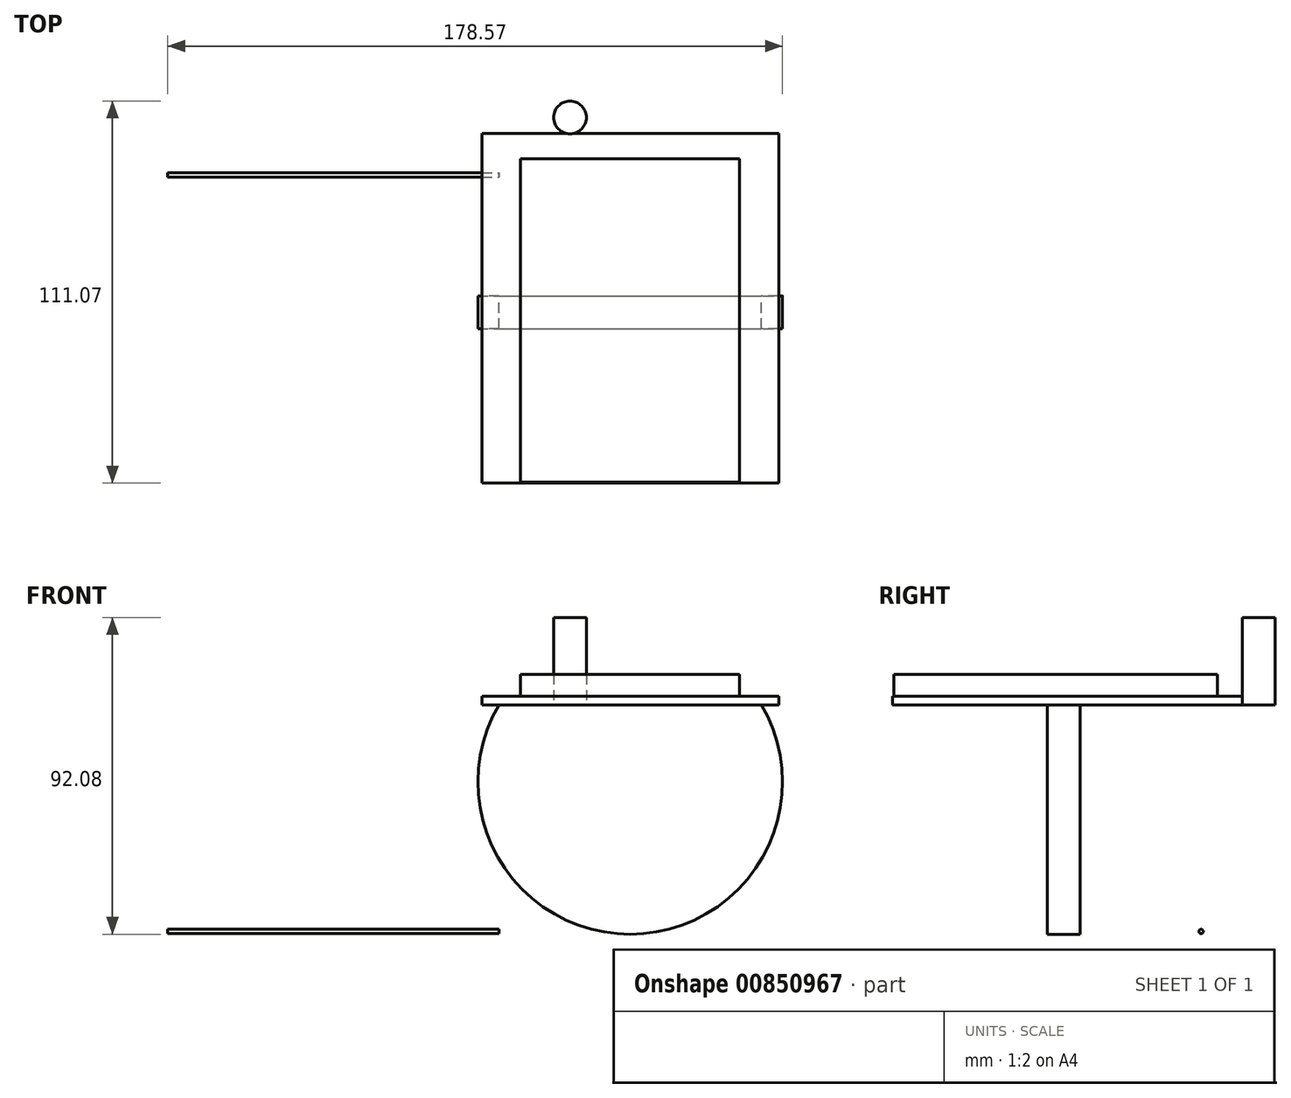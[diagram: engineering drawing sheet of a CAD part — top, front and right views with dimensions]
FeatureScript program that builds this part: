
annotation { "Feature Type Name" : "Feature", "Feature Type Description" : "" }
export const myFeature = defineFeature(function(context is Context, id is Id, definition is map)
    precondition{}
    {
        {
            var Q0;
            Q0=qCreatedBy(makeId("Front.planeOp"),FACE);
            var sketch = newSketch(context, id + "F0", { "sketchPlane" : qUnion([Q0])});
            skArc(sketch, "E0", {"start": v(0, 0) * mm, "mid": v(38.09, -66.68) * mm, "end": v(76.17, 0) * mm});
            skLineSegment(sketch, "E1", {"start": v(0, 0) * mm, "end": v(76.17, 0) * mm});
            skSolve(sketch);
        }
        {
            var Q0;
            Q0 = qSketchRegion(id + "F0", true);
            extrude(context, id + "F1", {"entities" : qUnion([Q0]), "depth" : 9.52 * mm, "offsetDistance" : 25.4 * mm});
        }
        {
            var Q0;
            Q0=makeQuery(id+"F1.opExtrude","SWEPT_FACE",FACE,{"disambiguationData":[OSD([sQuery(id+"F0.wireOp",EDGE,"E1")])]});
            var sketch = newSketch(context, id + "F2", { "sketchPlane" : qUnion([Q0])});
            skLineSegment(sketch, "E2.bottom", {"start": v(81.21, -54.44) * mm, "end": v(-5.02, -54.44) * mm});
            skLineSegment(sketch, "E2.top", {"start": v(81.21, 47.16) * mm, "end": v(-5.02, 47.16) * mm});
            skLineSegment(sketch, "E2.left", {"start": v(81.21, -54.44) * mm, "end": v(81.21, 47.16) * mm});
            skLineSegment(sketch, "E2.right", {"start": v(-5.02, -54.44) * mm, "end": v(-5.02, 47.16) * mm});
            skSolve(sketch);
        }
        {
            var Q0;
            Q0=makeQuery(id+"F2.imprint","IMPRINT",FACE,{"disambiguationData":[TD([[makeQuery(id+"F2.imprint","IMPRINT",EDGE,{"derivedFrom":sQuery(id+"F2.wireOp",EDGE,"E2.bottom")}),-1.0]])]});
            var Q1;
            {var subQ0=sQuery(id+"F0.wireOp",EDGE,"E1");Q1=makeQuery(id+"F2.imprint","IMPRINT",FACE,{"disambiguationData":[TD([[makeQuery(id+"F2.imprint","IMPRINT",EDGE,{"derivedFrom":makeQuery(id+"F1.opExtrude","CAP_EDGE",EDGE,{"disambiguationData":[OSD([subQ0])],"isStart":true})}),-1.0]])]});}
            extrude(context, id + "F3", {"entities" : qUnion([Q0, Q1]), "depth" : 2.54 * mm, "offsetDistance" : 25.4 * mm});
        }
        {
            var Q0;
            Q0=makeQuery(id+"F3.opExtrude","CAP_FACE",FACE,{"disambiguationData":[OSD([sQuery(id+"F2.wireOp",EDGE,"E2.bottom"),sQuery(id+"F2.wireOp",EDGE,"E2.top"),sQuery(id+"F2.wireOp",EDGE,"E2.left"),sQuery(id+"F2.wireOp",EDGE,"E2.right")])],"isStart":false});
            var sketch = newSketch(context, id + "F4", { "sketchPlane" : qUnion([Q0])});
            skLineSegment(sketch, "E3.bottom", {"start": v(69.76, -54.14) * mm, "end": v(6.26, -54.14) * mm});
            skLineSegment(sketch, "E3.top", {"start": v(69.76, 39.84) * mm, "end": v(6.26, 39.84) * mm});
            skLineSegment(sketch, "E3.left", {"start": v(69.76, -54.14) * mm, "end": v(69.76, 39.84) * mm});
            skLineSegment(sketch, "E3.right", {"start": v(6.26, -54.14) * mm, "end": v(6.26, 39.84) * mm});
            skSolve(sketch);
        }
        {
            var Q0;
            Q0=makeQuery(id+"F4.imprint","IMPRINT",FACE,{"disambiguationData":[TD([[makeQuery(id+"F4.imprint","IMPRINT",EDGE,{"derivedFrom":sQuery(id+"F4.wireOp",EDGE,"E3.bottom")}),-1.0]])]});
            extrude(context, id + "F5", {"entities" : qUnion([Q0]), "depth" : 6.35 * mm, "offsetDistance" : 25.4 * mm});
        }
        {
            var Q0;
            Q0=qCreatedBy(makeId("Top.planeOp"),FACE);
            var sketch = newSketch(context, id + "F6", { "sketchPlane" : qUnion([Q0])});
            skCircle(sketch, "E4", {"center": v(20.6, 51.86) * mm, "radius": 4.76 * mm});
            skSolve(sketch);
        }
        {
            var Q0;
            Q0=makeQuery(id+"F6.imprint","IMPRINT",FACE,{"disambiguationData":[TD([[makeQuery(id+"F6.imprint","IMPRINT",EDGE,{"derivedFrom":sQuery(id+"F6.wireOp",EDGE,"E4")}),1.0]])]});
            extrude(context, id + "F7", {"entities" : qUnion([Q0]), "depth" : 25.4 * mm, "offsetDistance" : 25.4 * mm});
        }
        {
            var Q0;
            Q0=qCreatedBy(makeId("Right.planeOp"),FACE);
            var sketch = newSketch(context, id + "F8", { "sketchPlane" : qUnion([Q0])});
            skCircle(sketch, "E5", {"center": v(35.15, -65.9) * mm, "radius": 0.63 * mm});
            skSolve(sketch);
        }
        {
            var Q0;
            Q0 = qSketchRegion(id + "F8", true);
            extrude(context, id + "F9", {"entities" : qUnion([Q0]), "oppositeDirection" : true, "depth" : 96.27 * mm, "offsetDistance" : 25.4 * mm});
        }
    });
